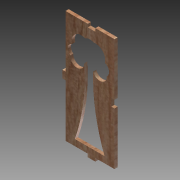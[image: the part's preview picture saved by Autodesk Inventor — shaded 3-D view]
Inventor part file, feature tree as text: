
AUTODESK INVENTOR PART (.ipt)
format: ipt  version: 2015 (Build 190159000, 159)  size: 175,616 bytes
history: native  units: in
note: dims shown in document units (in); Inventor stores cm internally (conversion verified against a paired STEP export)
features: extrude x4, sketch x4
ambient origin geometry x8: Origin, YZ Plane, XZ Plane, XY Plane, X Axis, Y Axis, Z Axis, Center Point
bodies: Solid1 (feature_tree)
feature tree (8):
  extrude  "Extrusion1"  Depth=1.959in
  sketch  "Sketch2"  dims[d2=0.125in d3=0.0in d4=0.15in]
  extrude  "Extrusion2"  Depth=0.125in
  extrude  "Extrusion3"  Depth=0.125in
  sketch  "Sketch3"  dims[d5=0.3in d6=0.125in]
  extrude  "Extrusion4"  Depth=0.3in
  sketch  "Sketch1"  dims[d0=4.5in d1=1.959in]
  sketch  "Sketch4"  dims[d7=0.15in d8=0.3in d9=0.125in d13=0.3in d15=0.125in d16=0.125in d17=0.0in d18=0.125in d19=0.0in d20=0.3in d22=0.125in d23=2.8125in d24=0.25in d25=7.0in d26=0.25in d28=7.0in d29=1.041in d30=2.8125in d31=1.0in d32=0.0in d33=0.15in d34=1.041in d35=1.041in d36=0.15in]
